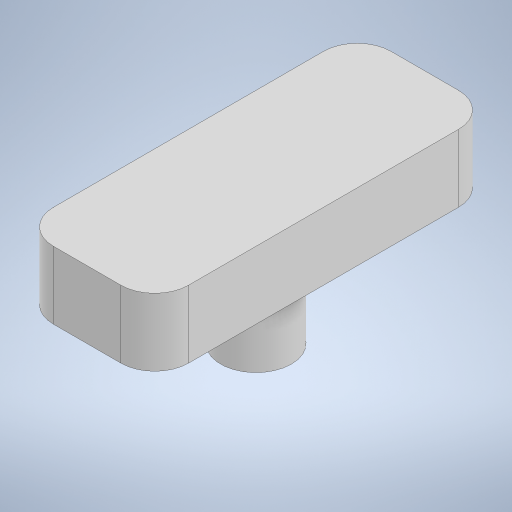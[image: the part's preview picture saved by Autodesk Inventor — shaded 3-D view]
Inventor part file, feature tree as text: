
AUTODESK INVENTOR PART (.ipt)
format: ipt  version: 2023.1 (Build 271208000, 208)  size: 205,824 bytes
history: native  units: mm
features: extrude x2, sketch x1
ambient origin geometry x8: Origin, YZ Plane, XZ Plane, XY Plane, X Axis, Y Axis, Z Axis, Center Point
bodies: Solid1 (feature_tree)
feature tree (3):
  sketch  "Sketch1"  dims[d0=2.5mm d1=4.0mm d2=10.0mm d3=0.999995mm d4=2.0mm d5=3.5mm d7=1.001258mm d13=5.0mm d18=2.0mm d19=0.0mm d20=0.2mm d21=2.5mm d22=0.0mm]
  extrude  "Extrusion1"  Depth=10.0mm
  extrude  "Extrusion2"  Depth=2.5mm
